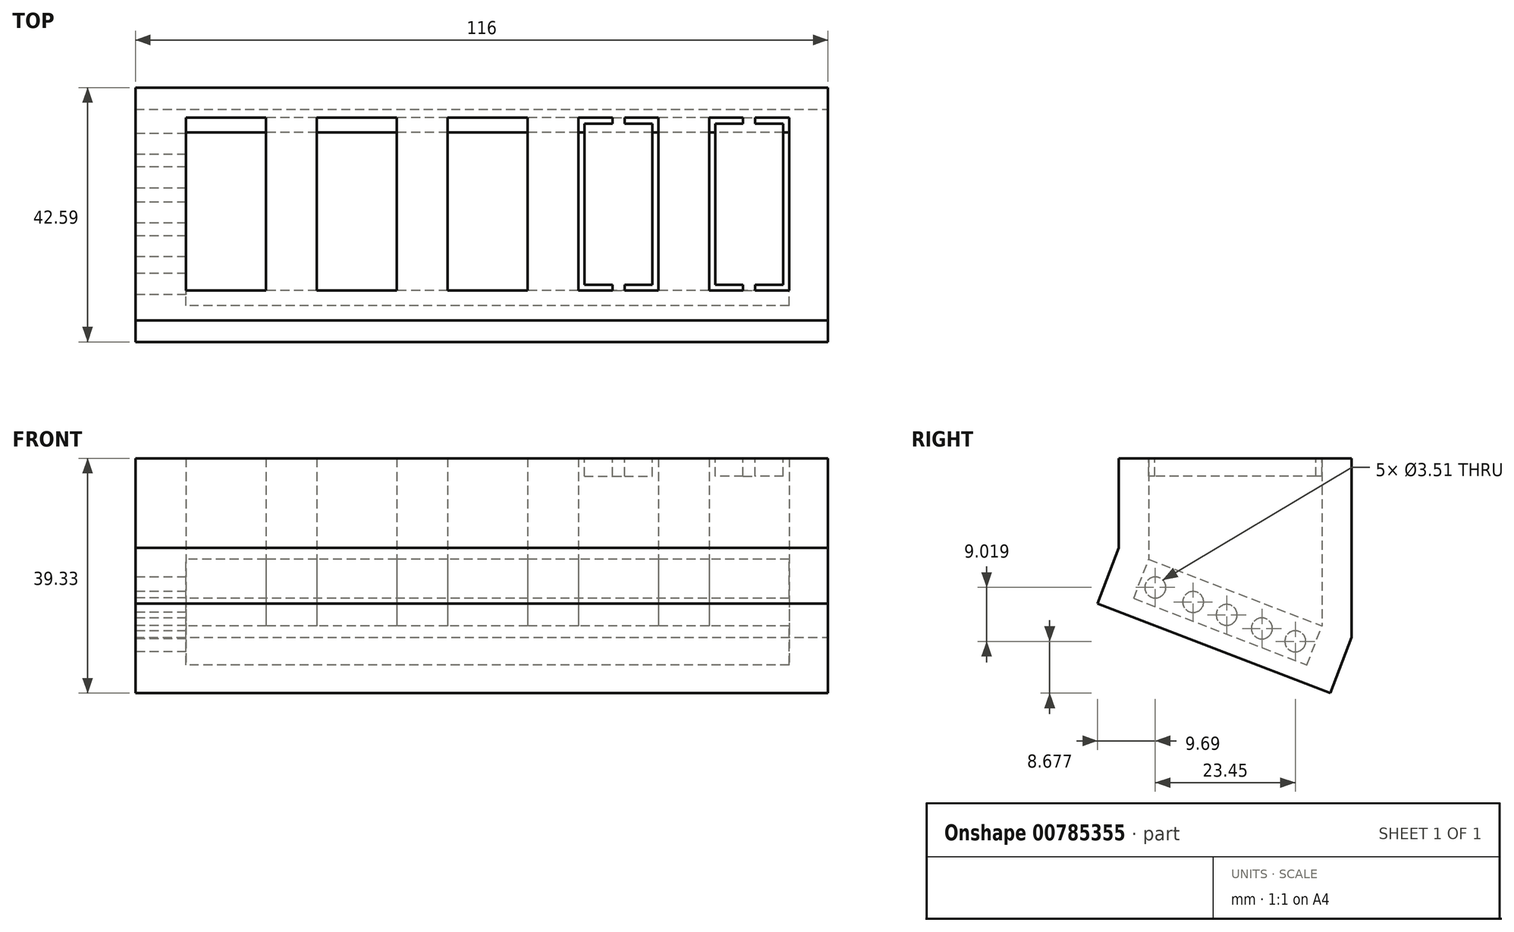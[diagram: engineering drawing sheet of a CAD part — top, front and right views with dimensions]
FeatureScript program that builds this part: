
annotation { "Feature Type Name" : "Feature", "Feature Type Description" : "" }
export const myFeature = defineFeature(function(context is Context, id is Id, definition is map)
    precondition{}
    {
        {
            var Q0;
            Q0=qCreatedBy(makeId("Top.planeOp"),FACE);
            var sketch = newSketch(context, id + "F0", { "sketchPlane" : qUnion([Q0])});
            skLineSegment(sketch, "E0.bottom", {"start": v(-68.44, 15.05) * mm, "end": v(47.56, 15.05) * mm});
            skLineSegment(sketch, "E0.top", {"start": v(-68.44, -23.95) * mm, "end": v(47.56, -23.95) * mm});
            skLineSegment(sketch, "E0.left", {"start": v(-68.44, 15.05) * mm, "end": v(-68.44, -23.95) * mm});
            skLineSegment(sketch, "E0.right", {"start": v(47.56, 15.05) * mm, "end": v(47.56, -23.95) * mm});
            skLineSegment(sketch, "E1.bottom", {"start": v(-59.94, 10.05) * mm, "end": v(-46.54, 10.05) * mm});
            skLineSegment(sketch, "E1.top", {"start": v(-59.94, -18.95) * mm, "end": v(-46.54, -18.95) * mm});
            skLineSegment(sketch, "E1.left", {"start": v(-59.94, 10.05) * mm, "end": v(-59.94, -18.95) * mm});
            skLineSegment(sketch, "E1.right", {"start": v(-46.54, 10.05) * mm, "end": v(-46.54, -18.95) * mm});
            skPoint(sketch, "E2", {"position": v(-46.54, -4.45) * mm});
            skPoint(sketch, "E3.startSnap0", {"position": v(-68.44, -4.45) * mm});
            skLineSegment(sketch, "E4.bottom", {"start": v(-38.04, 10.05) * mm, "end": v(-24.64, 10.05) * mm});
            skLineSegment(sketch, "E4.top", {"start": v(-38.04, -18.95) * mm, "end": v(-24.64, -18.95) * mm});
            skLineSegment(sketch, "E4.left", {"start": v(-38.04, 10.05) * mm, "end": v(-38.04, -18.95) * mm});
            skLineSegment(sketch, "E4.right", {"start": v(-24.64, 10.05) * mm, "end": v(-24.64, -18.95) * mm});
            skPoint(sketch, "E5", {"position": v(-24.64, -4.45) * mm});
            skLineSegment(sketch, "E6.bottom", {"start": v(-16.14, 10.05) * mm, "end": v(-2.74, 10.05) * mm});
            skLineSegment(sketch, "E6.top", {"start": v(-16.14, -18.95) * mm, "end": v(-2.74, -18.95) * mm});
            skLineSegment(sketch, "E6.left", {"start": v(-16.14, 10.05) * mm, "end": v(-16.14, -18.95) * mm});
            skLineSegment(sketch, "E6.right", {"start": v(-2.74, 10.05) * mm, "end": v(-2.74, -18.95) * mm});
            skPoint(sketch, "E7", {"position": v(-2.74, -4.45) * mm});
            skLineSegment(sketch, "E8", {"start": v(-46.54, -4.45) * mm, "end": v(-38.04, -4.45) * mm});
            skLineSegment(sketch, "E9", {"start": v(-24.64, -4.45) * mm, "end": v(-16.14, -4.45) * mm});
            skLineSegment(sketch, "E10.bottom", {"start": v(5.76, 10.05) * mm, "end": v(19.16, 10.05) * mm});
            skLineSegment(sketch, "E10.top", {"start": v(5.76, -18.95) * mm, "end": v(19.16, -18.95) * mm});
            skLineSegment(sketch, "E10.left", {"start": v(5.76, 10.05) * mm, "end": v(5.76, -18.95) * mm});
            skLineSegment(sketch, "E10.right", {"start": v(19.16, 10.05) * mm, "end": v(19.16, -18.95) * mm});
            skPoint(sketch, "E11", {"position": v(19.16, -4.45) * mm});
            skLineSegment(sketch, "E12", {"start": v(-2.74, -4.45) * mm, "end": v(5.76, -4.45) * mm});
            skLineSegment(sketch, "E13.bottom", {"start": v(27.66, 10.05) * mm, "end": v(41.06, 10.05) * mm});
            skLineSegment(sketch, "E13.top", {"start": v(27.66, -18.95) * mm, "end": v(41.06, -18.95) * mm});
            skLineSegment(sketch, "E13.left", {"start": v(27.66, 10.05) * mm, "end": v(27.66, -18.95) * mm});
            skLineSegment(sketch, "E13.right", {"start": v(41.06, 10.05) * mm, "end": v(41.06, -18.95) * mm});
            skPoint(sketch, "E14", {"position": v(41.06, -4.45) * mm});
            skLineSegment(sketch, "E15", {"start": v(19.16, -4.45) * mm, "end": v(27.66, -4.45) * mm});
            skLineSegment(sketch, "E16", {"start": v(-68.44, -4.45) * mm, "end": v(-59.94, -4.45) * mm, "construction": true});
            skLineSegment(sketch, "E17", {"start": v(41.06, -4.45) * mm, "end": v(47.56, -4.45) * mm, "construction": true});
            skSolve(sketch);
        }
        {
            var Q0;
            Q0=makeQuery(id+"F0.imprint","IMPRINT",FACE,{"disambiguationData":[TD([[makeQuery(id+"F0.imprint","IMPRINT",EDGE,{"derivedFrom":sQuery(id+"F0.wireOp",EDGE,"E0.bottom")}),-1.0]])]});
            extrude(context, id + "F1", {"entities" : qUnion([Q0]), "depth" : 30 * mm, "offsetDistance" : 25 * mm});
        }
        {
            var Q0;
            Q0=makeQuery(id+"F1.opExtrude","SWEPT_FACE",FACE,{"disambiguationData":[OSD([sQuery(id+"F0.wireOp",EDGE,"E0.left")])]});
            var sketch = newSketch(context, id + "F2", { "sketchPlane" : qUnion([Q0])});
            skLineSegment(sketch, "E18.0", {"start": v(-15.05, 30) * mm, "end": v(-15.05, 0) * mm});
            skLineSegment(sketch, "E18.1", {"start": v(23.95, 30) * mm, "end": v(23.95, 0) * mm});
            skLineSegment(sketch, "E18.2", {"start": v(-15.05, 0) * mm, "end": v(23.95, 0) * mm});
            skLineSegment(sketch, "E19", {"start": v(-15.05, 0) * mm, "end": v(23.95, 15) * mm});
            skSolve(sketch);
        }
        {
            var Q0;
            {var subQ0=sQuery(id+"F2.wireOp",EDGE,"E18.2");Q0=makeQuery(id+"F2.imprint","IMPRINT",FACE,{"disambiguationData":[TD([[makeQuery(id+"F2.imprint","IMPRINT",EDGE,{"derivedFrom":subQ0}),1.0]])]});}
            extrude(context, id + "F3", {"entities" : qUnion([Q0]), "operationType" : NewBodyOperationType.REMOVE, "oppositeDirection" : true, "depth" : 121.2 * mm, "offsetDistance" : 25 * mm});
        }
        {
            var Q0;
            Q0=makeQuery(id+"F3.boolean.opBoolean","COPY",FACE,{"derivedFrom":makeQuery(id+"F3.opExtrude","SWEPT_FACE",FACE,{"disambiguationData":[OSD([sQuery(id+"F2.wireOp",EDGE,"E19")])]})});
            var sketch = newSketch(context, id + "F4", { "sketchPlane" : qUnion([Q0])});
            skLineSegment(sketch, "E20.0", {"start": v(-68.44, -14.04) * mm, "end": v(-68.44, 27.74) * mm});
            skLineSegment(sketch, "E20.1", {"start": v(47.56, 27.74) * mm, "end": v(47.56, -14.04) * mm});
            skLineSegment(sketch, "E20.2", {"start": v(47.56, 27.74) * mm, "end": v(-68.44, 27.74) * mm});
            skLineSegment(sketch, "E20.3", {"start": v(-68.44, -14.04) * mm, "end": v(47.56, -14.04) * mm});
            skLineSegment(sketch, "E20.4", {"start": v(41.06, -8.69) * mm, "end": v(-59.94, -8.69) * mm});
            skLineSegment(sketch, "E20.5", {"start": v(41.06, 22.39) * mm, "end": v(41.06, -8.69) * mm});
            skLineSegment(sketch, "E20.6", {"start": v(41.06, 22.39) * mm, "end": v(-59.94, 22.39) * mm});
            skLineSegment(sketch, "E20.7", {"start": v(-59.94, 22.39) * mm, "end": v(-59.94, -8.69) * mm});
            skPoint(sketch, "E21.orphan", {"position": v(27.66, 22.39) * mm});
            skPoint(sketch, "E22.orphan", {"position": v(27.66, -8.69) * mm});
            skSolve(sketch);
        }
        {
            var Q0;
            Q0=makeQuery(id+"F4.imprint","IMPRINT",FACE,{"disambiguationData":[TD([[makeQuery(id+"F4.imprint","IMPRINT",EDGE,{"derivedFrom":sQuery(id+"F4.wireOp",EDGE,"E20.0")}),-1.0]])]});
            extrude(context, id + "F5", {"entities" : qUnion([Q0]), "operationType" : NewBodyOperationType.ADD, "depth" : 10 * mm, "offsetDistance" : 25 * mm});
        }
        {
            var Q0;
            Q0=makeQuery(id+"F5.opExtrude","CAP_FACE",FACE,{"disambiguationData":[OSD([sQuery(id+"F4.wireOp",EDGE,"E20.0"),sQuery(id+"F4.wireOp",EDGE,"E20.1"),sQuery(id+"F4.wireOp",EDGE,"E20.2"),sQuery(id+"F4.wireOp",EDGE,"E20.3"),sQuery(id+"F4.wireOp",EDGE,"E20.4"),sQuery(id+"F4.wireOp",EDGE,"E20.5"),sQuery(id+"F4.wireOp",EDGE,"E20.6"),sQuery(id+"F4.wireOp",EDGE,"E20.7")])],"isStart":false});
            var sketch = newSketch(context, id + "F6", { "sketchPlane" : qUnion([Q0])});
            skLineSegment(sketch, "E23.0", {"start": v(-59.94, 22.39) * mm, "end": v(-59.94, -8.69) * mm});
            skLineSegment(sketch, "E23.1", {"start": v(41.06, 22.39) * mm, "end": v(-59.94, 22.39) * mm});
            skLineSegment(sketch, "E23.2", {"start": v(41.06, -8.69) * mm, "end": v(-59.94, -8.69) * mm});
            skLineSegment(sketch, "E23.3", {"start": v(41.06, 22.39) * mm, "end": v(41.06, -8.69) * mm});
            skSolve(sketch);
        }
        {
            var Q0;
            Q0=makeQuery(id+"F6.imprint","IMPRINT",FACE,{"disambiguationData":[TD([[makeQuery(id+"F6.imprint","IMPRINT",EDGE,{"derivedFrom":sQuery(id+"F6.wireOp",EDGE,"E23.0")}),1.0]])]});
            extrude(context, id + "F7", {"entities" : qUnion([Q0]), "operationType" : NewBodyOperationType.ADD, "oppositeDirection" : true, "depth" : 3 * mm, "offsetDistance" : 25 * mm});
        }
        {
            var Q0;
            Q0=makeQuery(id+"F5.boolean.opBoolean","MERGE",FACE,{"derivedFrom":[makeQuery(id+"F1.opExtrude","SWEPT_FACE",FACE,{"disambiguationData":[OSD([sQuery(id+"F0.wireOp",EDGE,"E0.left")])]}),makeQuery(id+"F5.opExtrude","SWEPT_FACE",FACE,{"disambiguationData":[OSD([sQuery(id+"F4.wireOp",EDGE,"E20.0")])]})]});
            var sketch = newSketch(context, id + "F8", { "sketchPlane" : qUnion([Q0])});
            skLineSegment(sketch, "E24.0", {"start": v(27.54, 5.67) * mm, "end": v(25.4, 11.27) * mm});
            skLineSegment(sketch, "E24.1", {"start": v(-11.46, -9.33) * mm, "end": v(27.54, 5.67) * mm});
            skLineSegment(sketch, "E25", {"start": v(25.4, 11.27) * mm, "end": v(-13.6, -3.73) * mm, "construction": true});
            skCircle(sketch, "E26", {"center": v(5.9, 3.77) * mm, "radius": 1.76 * mm});
            skCircle(sketch, "E27", {"center": v(17.85, 8.37) * mm, "radius": 1.76 * mm});
            skCircle(sketch, "E28", {"center": v(-5.6, -0.65) * mm, "radius": 1.76 * mm});
            skCircle(sketch, "E29", {"center": v(0, 1.5) * mm, "radius": 1.76 * mm});
            skCircle(sketch, "E30", {"center": v(11.52, 5.93) * mm, "radius": 1.76 * mm});
            skSolve(sketch);
        }
        {
            var Q0;
            Q0=makeQuery(id+"F8.imprint","IMPRINT",FACE,{"disambiguationData":[TD([[makeQuery(id+"F8.imprint","IMPRINT",EDGE,{"derivedFrom":sQuery(id+"F8.wireOp",EDGE,"E28")}),1.0]])]});
            var Q1;
            Q1=makeQuery(id+"F8.imprint","IMPRINT",FACE,{"disambiguationData":[TD([[makeQuery(id+"F8.imprint","IMPRINT",EDGE,{"derivedFrom":sQuery(id+"F8.wireOp",EDGE,"E29")}),1.0]])]});
            var Q2;
            Q2=makeQuery(id+"F8.imprint","IMPRINT",FACE,{"disambiguationData":[TD([[makeQuery(id+"F8.imprint","IMPRINT",EDGE,{"derivedFrom":sQuery(id+"F8.wireOp",EDGE,"E26")}),1.0]])]});
            var Q3;
            Q3=makeQuery(id+"F8.imprint","IMPRINT",FACE,{"disambiguationData":[TD([[makeQuery(id+"F8.imprint","IMPRINT",EDGE,{"derivedFrom":sQuery(id+"F8.wireOp",EDGE,"E30")}),1.0]])]});
            var Q4;
            Q4=makeQuery(id+"F8.imprint","IMPRINT",FACE,{"disambiguationData":[TD([[makeQuery(id+"F8.imprint","IMPRINT",EDGE,{"derivedFrom":sQuery(id+"F8.wireOp",EDGE,"E27")}),1.0]])]});
            extrude(context, id + "F9", {"entities" : qUnion([Q0, Q1, Q2, Q3, Q4]), "operationType" : NewBodyOperationType.REMOVE, "oppositeDirection" : true, "depth" : 25 * mm, "offsetDistance" : 25 * mm});
        }
        {
            var Q0;
            Q0=makeQuery(id+"F1.opExtrude","CAP_FACE",FACE,{"disambiguationData":[OSD([sQuery(id+"F0.wireOp",EDGE,"E0.bottom"),sQuery(id+"F0.wireOp",EDGE,"E0.top"),sQuery(id+"F0.wireOp",EDGE,"E0.left"),sQuery(id+"F0.wireOp",EDGE,"E0.right"),sQuery(id+"F0.wireOp",EDGE,"E1.bottom"),sQuery(id+"F0.wireOp",EDGE,"E1.top"),sQuery(id+"F0.wireOp",EDGE,"E1.left"),sQuery(id+"F0.wireOp",EDGE,"E1.right"),sQuery(id+"F0.wireOp",EDGE,"E4.bottom"),sQuery(id+"F0.wireOp",EDGE,"E4.top"),sQuery(id+"F0.wireOp",EDGE,"E4.left"),sQuery(id+"F0.wireOp",EDGE,"E4.right"),sQuery(id+"F0.wireOp",EDGE,"E6.bottom"),sQuery(id+"F0.wireOp",EDGE,"E6.top"),sQuery(id+"F0.wireOp",EDGE,"E6.left"),sQuery(id+"F0.wireOp",EDGE,"E6.right"),sQuery(id+"F0.wireOp",EDGE,"E10.bottom"),sQuery(id+"F0.wireOp",EDGE,"E10.top"),sQuery(id+"F0.wireOp",EDGE,"E10.left"),sQuery(id+"F0.wireOp",EDGE,"E10.right"),sQuery(id+"F0.wireOp",EDGE,"E13.bottom"),sQuery(id+"F0.wireOp",EDGE,"E13.top"),sQuery(id+"F0.wireOp",EDGE,"E13.left"),sQuery(id+"F0.wireOp",EDGE,"E13.right")])],"isStart":false});
            var sketch = newSketch(context, id + "F10", { "sketchPlane" : qUnion([Q0])});
            skLineSegment(sketch, "E31.0", {"start": v(5.76, 10.05) * mm, "end": v(5.76, -18.95) * mm});
            skLineSegment(sketch, "E31.1", {"start": v(5.76, 10.05) * mm, "end": v(19.16, 10.05) * mm});
            skLineSegment(sketch, "E31.2", {"start": v(19.16, 10.05) * mm, "end": v(19.16, -18.95) * mm});
            skLineSegment(sketch, "E31.3", {"start": v(5.76, -18.95) * mm, "end": v(19.16, -18.95) * mm});
            skLineSegment(sketch, "E31.4", {"start": v(27.66, 10.05) * mm, "end": v(41.06, 10.05) * mm});
            skLineSegment(sketch, "E31.5", {"start": v(27.66, 10.05) * mm, "end": v(27.66, -18.95) * mm});
            skLineSegment(sketch, "E31.6", {"start": v(27.66, -18.95) * mm, "end": v(41.06, -18.95) * mm});
            skLineSegment(sketch, "E31.7", {"start": v(41.06, 10.05) * mm, "end": v(41.06, -18.95) * mm});
            skLineSegment(sketch, "E32.0", {"start": v(6.76, -17.95) * mm, "end": v(18.16, -17.95) * mm});
            skLineSegment(sketch, "E32.1", {"start": v(6.76, 9.05) * mm, "end": v(6.76, -17.95) * mm});
            skLineSegment(sketch, "E32.2", {"start": v(6.76, 9.05) * mm, "end": v(18.16, 9.05) * mm});
            skLineSegment(sketch, "E32.3", {"start": v(18.16, 9.05) * mm, "end": v(18.16, -17.95) * mm});
            skPoint(sketch, "E33", {"position": v(12.46, 9.05) * mm});
            skLineSegment(sketch, "E34", {"start": v(11.49, 10.05) * mm, "end": v(11.49, 9.05) * mm});
            skLineSegment(sketch, "E35", {"start": v(13.49, 10.05) * mm, "end": v(13.49, 9.05) * mm});
            skLineSegment(sketch, "E36", {"start": v(11.49, -17.95) * mm, "end": v(11.49, -18.95) * mm});
            skLineSegment(sketch, "E37", {"start": v(13.49, -17.95) * mm, "end": v(13.49, -18.95) * mm});
            skLineSegment(sketch, "E38", {"start": v(19.16, 10.05) * mm, "end": v(27.66, 10.05) * mm, "construction": true});
            skPoint(sketch, "E39", {"position": v(23.41, 10.05) * mm});
            skLineSegment(sketch, "E40", {"start": v(23.41, 12.2) * mm, "end": v(23.41, -21.9) * mm, "construction": true});
            skLineSegment(sketch, "E41.MirrorCS", {"start": v(28.66, 9.05) * mm, "end": v(28.66, -17.95) * mm});
            skLineSegment(sketch, "E42.MirrorCS", {"start": v(40.06, -17.95) * mm, "end": v(28.66, -17.95) * mm});
            skLineSegment(sketch, "E43.MirrorCS", {"start": v(33.34, -17.95) * mm, "end": v(33.34, -18.95) * mm});
            skLineSegment(sketch, "E44.MirrorCS", {"start": v(35.34, -17.95) * mm, "end": v(35.34, -18.95) * mm});
            skLineSegment(sketch, "E45.MirrorCS", {"start": v(40.06, 9.05) * mm, "end": v(40.06, -17.95) * mm});
            skLineSegment(sketch, "E46.MirrorCS", {"start": v(40.06, 9.05) * mm, "end": v(28.66, 9.05) * mm});
            skLineSegment(sketch, "E47.MirrorCS", {"start": v(35.34, 10.05) * mm, "end": v(35.34, 9.05) * mm});
            skLineSegment(sketch, "E48.MirrorCS", {"start": v(33.34, 10.05) * mm, "end": v(33.34, 9.05) * mm});
            skSolve(sketch);
        }
        {
            var Q0;
            {var subQ1=sQuery(id+"F10.wireOp",EDGE,"E41.MirrorCS");Q0=makeQuery(id+"F10.imprint","IMPRINT",FACE,{"disambiguationData":[TD([[makeQuery(id+"F10.imprint","IMPRINT",EDGE,{"derivedFrom":subQ1}),1.0]])]});}
            var Q1;
            {var subQ0=sQuery(id+"F10.wireOp",EDGE,"E32.1");Q1=makeQuery(id+"F10.imprint","IMPRINT",FACE,{"disambiguationData":[TD([[makeQuery(id+"F10.imprint","IMPRINT",EDGE,{"derivedFrom":subQ0}),1.0]])]});}
            var Q2;
            {var subQ0=sQuery(id+"F10.wireOp",EDGE,"E34");Q2=makeQuery(id+"F10.imprint","IMPRINT",FACE,{"disambiguationData":[TD([[makeQuery(id+"F10.imprint","IMPRINT",EDGE,{"derivedFrom":subQ0}),1.0]])]});}
            var Q3;
            {var subQ0=sQuery(id+"F10.wireOp",EDGE,"E47.MirrorCS");Q3=makeQuery(id+"F10.imprint","IMPRINT",FACE,{"disambiguationData":[TD([[makeQuery(id+"F10.imprint","IMPRINT",EDGE,{"derivedFrom":subQ0}),-1.0]])]});}
            var Q4;
            {var subQ0=sQuery(id+"F10.wireOp",EDGE,"E36");Q4=makeQuery(id+"F10.imprint","IMPRINT",FACE,{"disambiguationData":[TD([[makeQuery(id+"F10.imprint","IMPRINT",EDGE,{"derivedFrom":subQ0}),1.0]])]});}
            var Q5;
            {var subQ0=sQuery(id+"F10.wireOp",EDGE,"E43.MirrorCS");Q5=makeQuery(id+"F10.imprint","IMPRINT",FACE,{"disambiguationData":[TD([[makeQuery(id+"F10.imprint","IMPRINT",EDGE,{"derivedFrom":subQ0}),1.0]])]});}
            extrude(context, id + "F11", {"entities" : qUnion([Q0, Q1, Q2, Q3, Q4, Q5]), "operationType" : NewBodyOperationType.ADD, "oppositeDirection" : true, "depth" : 3 * mm, "offsetDistance" : 25 * mm});
        }
    });
